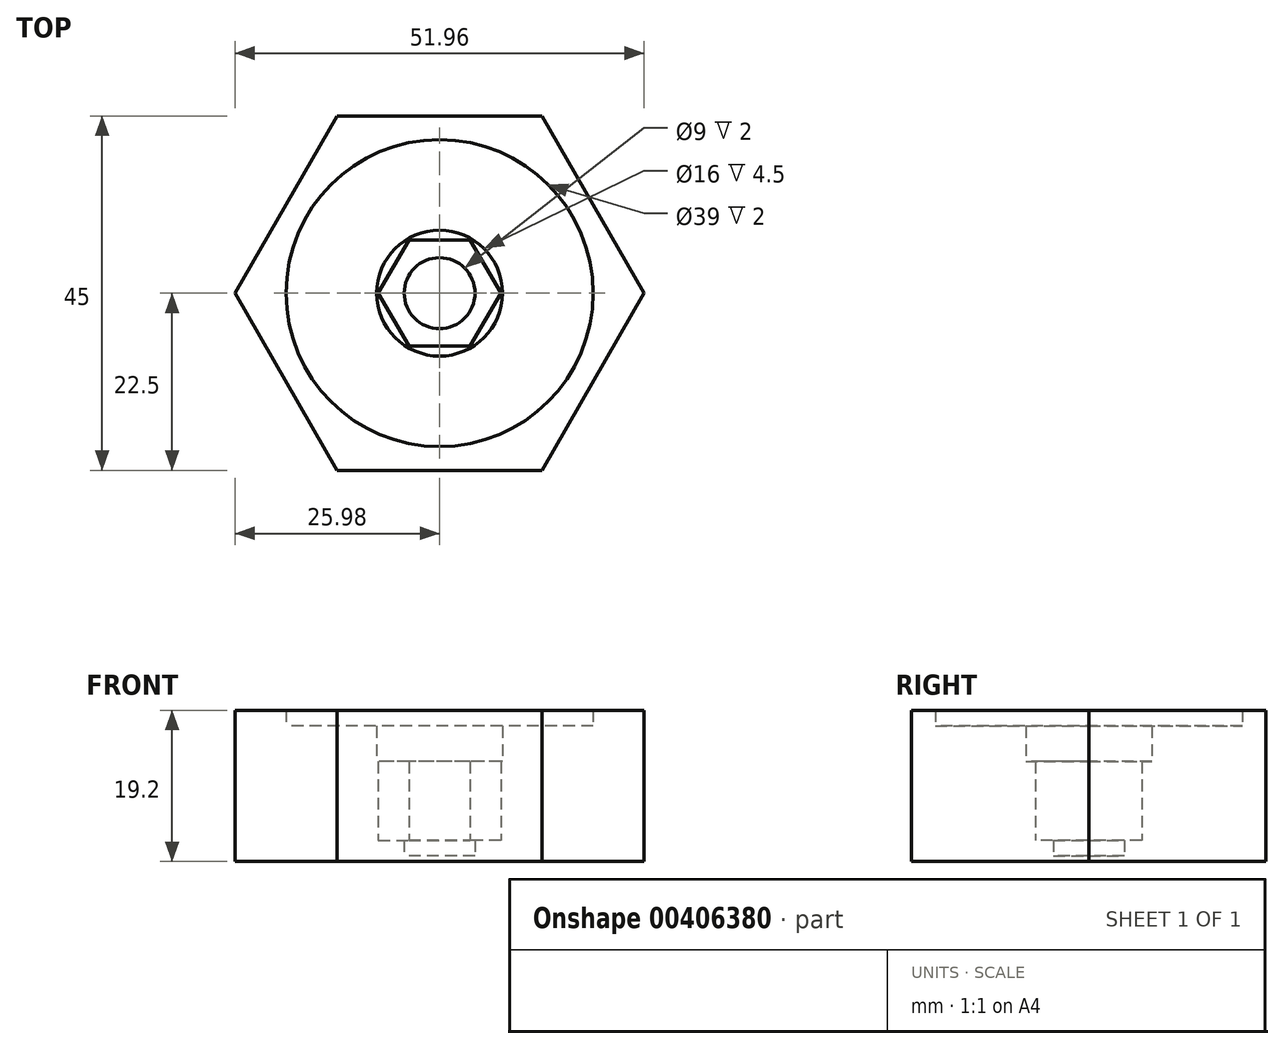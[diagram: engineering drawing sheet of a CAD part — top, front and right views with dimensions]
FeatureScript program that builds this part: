
annotation { "Feature Type Name" : "Feature", "Feature Type Description" : "" }
export const myFeature = defineFeature(function(context is Context, id is Id, definition is map)
    precondition{}
    {
        {
            var Q0;
            Q0=qCreatedBy(makeId("Top.planeOp"),FACE);
            var sketch = newSketch(context, id + "F0", { "sketchPlane" : qUnion([Q0])});
            skCircle(sketch, "E0.cCircle", {"center": v(0, 0) * mm, "radius": 22.5 * mm, "construction": true});
            skLineSegment(sketch, "E0.0", {"start": v(13, -22.5) * mm, "end": v(-13, -22.5) * mm});
            skLineSegment(sketch, "E0.1", {"start": v(-13, -22.5) * mm, "end": v(-25.98, 0) * mm});
            skLineSegment(sketch, "E0.2", {"start": v(-25.98, 0) * mm, "end": v(-13, 22.5) * mm});
            skLineSegment(sketch, "E0.3", {"start": v(-13, 22.5) * mm, "end": v(13, 22.5) * mm});
            skLineSegment(sketch, "E0.4", {"start": v(13, 22.5) * mm, "end": v(25.98, 0) * mm});
            skLineSegment(sketch, "E0.5", {"start": v(25.98, 0) * mm, "end": v(13, -22.5) * mm});
            skPoint(sketch, "E0.0.midPoint", {"position": v(0, -22.5) * mm});
            skSolve(sketch);
        }
        {
            var Q0;
            Q0=makeQuery(id+"F0.imprint","IMPRINT",FACE,{"disambiguationData":[TD([[makeQuery(id+"F0.imprint","IMPRINT",EDGE,{"derivedFrom":sQuery(id+"F0.wireOp",EDGE,"E0.0")}),-1.0]])]});
            extrude(context, id + "F1", {"entities" : qUnion([Q0]), "depth" : 0.7 * mm});
        }
        {
            var Q0;
            Q0=makeQuery(id+"F1.opExtrude","CAP_FACE",FACE,{"disambiguationData":[OSD([sQuery(id+"F0.wireOp",EDGE,"E0.0"),sQuery(id+"F0.wireOp",EDGE,"E0.1"),sQuery(id+"F0.wireOp",EDGE,"E0.2"),sQuery(id+"F0.wireOp",EDGE,"E0.3"),sQuery(id+"F0.wireOp",EDGE,"E0.4"),sQuery(id+"F0.wireOp",EDGE,"E0.5")])],"isStart":false});
            var sketch = newSketch(context, id + "F2", { "sketchPlane" : qUnion([Q0])});
            skCircle(sketch, "E1", {"center": v(0, 0) * mm, "radius": 4.5 * mm});
            skSolve(sketch);
        }
        {
            var Q0;
            Q0=makeQuery(id+"F2.imprint","IMPRINT",FACE,{"disambiguationData":[TD([[makeQuery(id+"F2.imprint","IMPRINT",EDGE,{"derivedFrom":sQuery(id+"F2.wireOp",EDGE,"E1")}),-1.0]])]});
            extrude(context, id + "F3", {"entities" : qUnion([Q0]), "operationType" : NewBodyOperationType.ADD, "depth" : 2 * mm});
        }
        {
            var Q0;
            Q0=makeQuery(id+"F3.opExtrude","CAP_FACE",FACE,{"disambiguationData":[OSD([sQuery(id+"F0.wireOp",EDGE,"E0.0"),sQuery(id+"F0.wireOp",EDGE,"E0.1"),sQuery(id+"F0.wireOp",EDGE,"E0.2"),sQuery(id+"F0.wireOp",EDGE,"E0.3"),sQuery(id+"F0.wireOp",EDGE,"E0.4"),sQuery(id+"F0.wireOp",EDGE,"E0.5"),sQuery(id+"F2.wireOp",EDGE,"E1")])],"isStart":false});
            var sketch = newSketch(context, id + "F4", { "sketchPlane" : qUnion([Q0])});
            skCircle(sketch, "E2.cCircle", {"center": v(0, 0) * mm, "radius": 6.75 * mm, "construction": true});
            skLineSegment(sketch, "E2.0", {"start": v(3.9, -6.75) * mm, "end": v(-3.9, -6.75) * mm});
            skLineSegment(sketch, "E2.1", {"start": v(-3.9, -6.75) * mm, "end": v(-7.8, 0) * mm});
            skLineSegment(sketch, "E2.2", {"start": v(-7.8, 0) * mm, "end": v(-3.9, 6.75) * mm});
            skLineSegment(sketch, "E2.3", {"start": v(-3.9, 6.75) * mm, "end": v(3.9, 6.75) * mm});
            skLineSegment(sketch, "E2.4", {"start": v(3.9, 6.75) * mm, "end": v(7.8, 0) * mm});
            skLineSegment(sketch, "E2.5", {"start": v(7.8, 0) * mm, "end": v(3.9, -6.75) * mm});
            skPoint(sketch, "E2.0.midPoint", {"position": v(0, -6.75) * mm});
            skSolve(sketch);
        }
        {
            var Q0;
            Q0=makeQuery(id+"F4.imprint","IMPRINT",FACE,{"disambiguationData":[TD([[makeQuery(id+"F4.imprint","IMPRINT",EDGE,{"derivedFrom":sQuery(id+"F4.wireOp",EDGE,"E2.0")}),1.0]])]});
            extrude(context, id + "F5", {"entities" : qUnion([Q0]), "operationType" : NewBodyOperationType.ADD, "depth" : 10 * mm});
        }
        {
            var Q0;
            Q0=makeQuery(id+"F5.opExtrude","CAP_FACE",FACE,{"disambiguationData":[OSD([sQuery(id+"F0.wireOp",EDGE,"E0.0"),sQuery(id+"F0.wireOp",EDGE,"E0.1"),sQuery(id+"F0.wireOp",EDGE,"E0.2"),sQuery(id+"F0.wireOp",EDGE,"E0.3"),sQuery(id+"F0.wireOp",EDGE,"E0.4"),sQuery(id+"F0.wireOp",EDGE,"E0.5"),sQuery(id+"F4.wireOp",EDGE,"E2.0"),sQuery(id+"F4.wireOp",EDGE,"E2.1"),sQuery(id+"F4.wireOp",EDGE,"E2.2"),sQuery(id+"F4.wireOp",EDGE,"E2.3"),sQuery(id+"F4.wireOp",EDGE,"E2.4"),sQuery(id+"F4.wireOp",EDGE,"E2.5")])],"isStart":false});
            var sketch = newSketch(context, id + "F6", { "sketchPlane" : qUnion([Q0])});
            skCircle(sketch, "E3", {"center": v(0, 0) * mm, "radius": 8 * mm});
            skSolve(sketch);
        }
        {
            var Q0;
            Q0=makeQuery(id+"F6.imprint","IMPRINT",FACE,{"disambiguationData":[TD([[makeQuery(id+"F6.imprint","IMPRINT",EDGE,{"derivedFrom":sQuery(id+"F6.wireOp",EDGE,"E3")}),-1.0]])]});
            extrude(context, id + "F7", {"entities" : qUnion([Q0]), "operationType" : NewBodyOperationType.ADD, "depth" : 4.5 * mm});
        }
        {
            var Q0;
            Q0=makeQuery(id+"F7.opExtrude","CAP_FACE",FACE,{"disambiguationData":[OSD([sQuery(id+"F0.wireOp",EDGE,"E0.0"),sQuery(id+"F0.wireOp",EDGE,"E0.1"),sQuery(id+"F0.wireOp",EDGE,"E0.2"),sQuery(id+"F0.wireOp",EDGE,"E0.3"),sQuery(id+"F0.wireOp",EDGE,"E0.4"),sQuery(id+"F0.wireOp",EDGE,"E0.5"),sQuery(id+"F6.wireOp",EDGE,"E3")])],"isStart":false});
            var sketch = newSketch(context, id + "F8", { "sketchPlane" : qUnion([Q0])});
            skCircle(sketch, "E4", {"center": v(0, 0) * mm, "radius": 19.5 * mm});
            skSolve(sketch);
        }
        {
            var Q0;
            Q0=makeQuery(id+"F8.imprint","IMPRINT",FACE,{"disambiguationData":[TD([[makeQuery(id+"F8.imprint","IMPRINT",EDGE,{"derivedFrom":sQuery(id+"F8.wireOp",EDGE,"E4")}),-1.0]])]});
            extrude(context, id + "F9", {"entities" : qUnion([Q0]), "operationType" : NewBodyOperationType.ADD, "depth" : 2 * mm});
        }
    });
